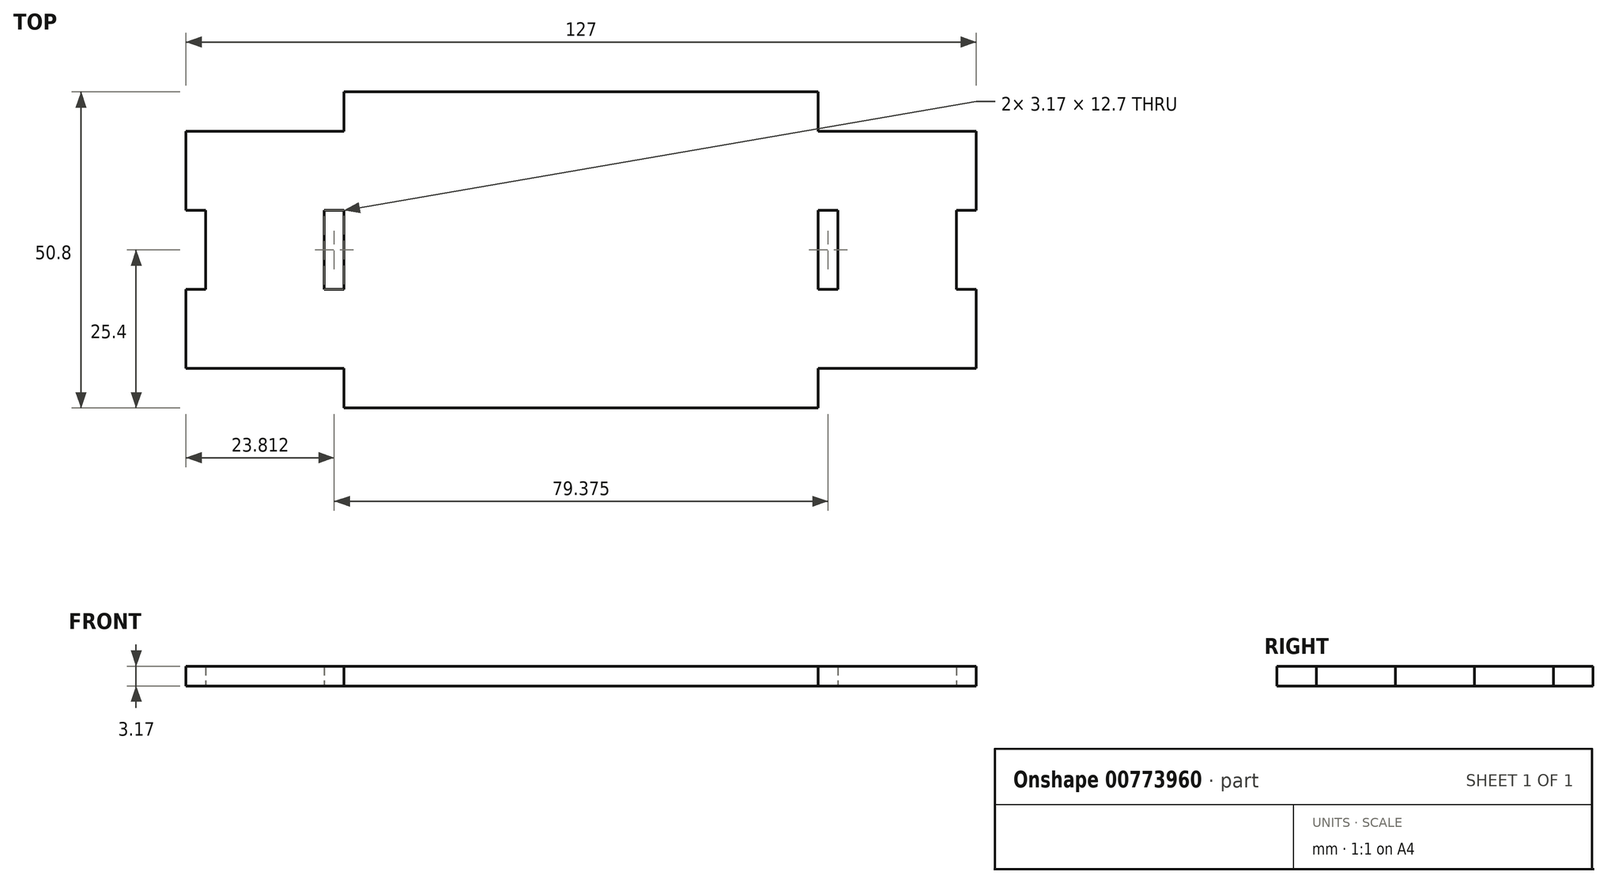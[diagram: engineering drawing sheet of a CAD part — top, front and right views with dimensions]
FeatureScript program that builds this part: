
annotation { "Feature Type Name" : "Feature", "Feature Type Description" : "" }
export const myFeature = defineFeature(function(context is Context, id is Id, definition is map)
    precondition{}
    {
        {
            var Q0;
            Q0=qCreatedBy(makeId("Top.planeOp"),FACE);
            var sketch = newSketch(context, id + "F0", { "sketchPlane" : qUnion([Q0])});
            skLineSegment(sketch, "E0.bottom", {"start": v(38.1, 25.4) * mm, "end": v(-38.1, 25.4) * mm});
            skLineSegment(sketch, "E0.top", {"start": v(38.1, -25.4) * mm, "end": v(-38.1, -25.4) * mm});
            skLineSegment(sketch, "E0.left", {"start": v(63.5, 19.05) * mm, "end": v(63.5, 6.35) * mm});
            skLineSegment(sketch, "E0.right", {"start": v(-63.5, 19.05) * mm, "end": v(-63.5, 6.35) * mm});
            skPoint(sketch, "E0.middle", {"position": v(0, 0) * mm});
            skLineSegment(sketch, "E1.right", {"start": v(-60.33, 6.35) * mm, "end": v(-60.33, -6.35) * mm});
            skLineSegment(sketch, "E2.bottom", {"start": v(-63.5, 6.35) * mm, "end": v(-60.33, 6.35) * mm});
            skLineSegment(sketch, "E2.top", {"start": v(-63.5, -6.35) * mm, "end": v(-60.33, -6.35) * mm});
            skLineSegment(sketch, "E3.trimOffspring", {"start": v(-63.5, -6.35) * mm, "end": v(-63.5, -19.44) * mm});
            skLineSegment(sketch, "E4.trimOffspring", {"start": v(-63.5, -6.35) * mm, "end": v(-63.5, -19.05) * mm});
            skLineSegment(sketch, "E5.MirrorCS", {"start": v(60.33, 6.35) * mm, "end": v(60.33, -6.35) * mm});
            skLineSegment(sketch, "E6.MirrorCS", {"start": v(63.5, 6.35) * mm, "end": v(60.33, 6.35) * mm});
            skLineSegment(sketch, "E7.MirrorCS", {"start": v(63.5, -6.35) * mm, "end": v(60.33, -6.35) * mm});
            skLineSegment(sketch, "E8.trimOffspring", {"start": v(63.5, -6.35) * mm, "end": v(63.5, -19.05) * mm});
            skLineSegment(sketch, "E9.bottom", {"start": v(-63.5, 19.05) * mm, "end": v(-38.1, 19.05) * mm});
            skLineSegment(sketch, "E9.right", {"start": v(-38.1, 19.05) * mm, "end": v(-38.1, 25.4) * mm});
            skLineSegment(sketch, "E10.MirrorCS", {"start": v(63.5, 19.05) * mm, "end": v(38.1, 19.05) * mm});
            skLineSegment(sketch, "E11.MirrorCS", {"start": v(38.1, 19.05) * mm, "end": v(38.1, 25.4) * mm});
            skLineSegment(sketch, "E12.MirrorCS", {"start": v(63.5, -19.05) * mm, "end": v(38.1, -19.05) * mm});
            skLineSegment(sketch, "E13.MirrorCS", {"start": v(38.1, -19.05) * mm, "end": v(38.1, -25.4) * mm});
            skLineSegment(sketch, "E14.MirrorCS", {"start": v(-38.1, -19.05) * mm, "end": v(-38.1, -25.4) * mm});
            skLineSegment(sketch, "E15.MirrorCS", {"start": v(-63.5, -19.05) * mm, "end": v(-38.1, -19.05) * mm});
            skLineSegment(sketch, "E16.bottom", {"start": v(-41.28, 6.35) * mm, "end": v(-38.1, 6.35) * mm});
            skLineSegment(sketch, "E16.top", {"start": v(-41.28, -6.35) * mm, "end": v(-38.1, -6.35) * mm});
            skLineSegment(sketch, "E16.left", {"start": v(-41.28, 6.35) * mm, "end": v(-41.28, -6.35) * mm});
            skLineSegment(sketch, "E16.right", {"start": v(-38.1, 6.35) * mm, "end": v(-38.1, -6.35) * mm});
            skLineSegment(sketch, "E17.MirrorCS", {"start": v(41.28, 6.35) * mm, "end": v(38.1, 6.35) * mm});
            skLineSegment(sketch, "E18.MirrorCS", {"start": v(41.28, 6.35) * mm, "end": v(41.28, -6.35) * mm});
            skLineSegment(sketch, "E19.MirrorCS", {"start": v(38.1, 6.35) * mm, "end": v(38.1, -6.35) * mm});
            skLineSegment(sketch, "E20.MirrorCS", {"start": v(41.28, -6.35) * mm, "end": v(38.1, -6.35) * mm});
            skSolve(sketch);
        }
        {
            var Q0;
            {var subQ21=sQuery(id+"F0.wireOp",EDGE,"StcgOun8-i1LN-XaPq-IhUf-35WJNKD1vWmb.top");Q0=makeQuery(id+"F0.imprint","IMPRINT",FACE,{"disambiguationData":[TD([[makeQuery(id+"F0.imprint","IMPRINT",EDGE,{"derivedFrom":subQ21}),1.0]])]});}
            var Q1;
            Q1=makeQuery(id+"F0.imprint","IMPRINT",FACE,{"disambiguationData":[TD([[makeQuery(id+"F0.imprint","IMPRINT",EDGE,{"derivedFrom":sQuery(id+"F0.wireOp",EDGE,"E0.bottom")}),1.0]])]});
            extrude(context, id + "F1", {"entities" : qUnion([Q0, Q1]), "depth" : 3.17 * mm, "offsetDistance" : 25.4 * mm});
        }
    });
